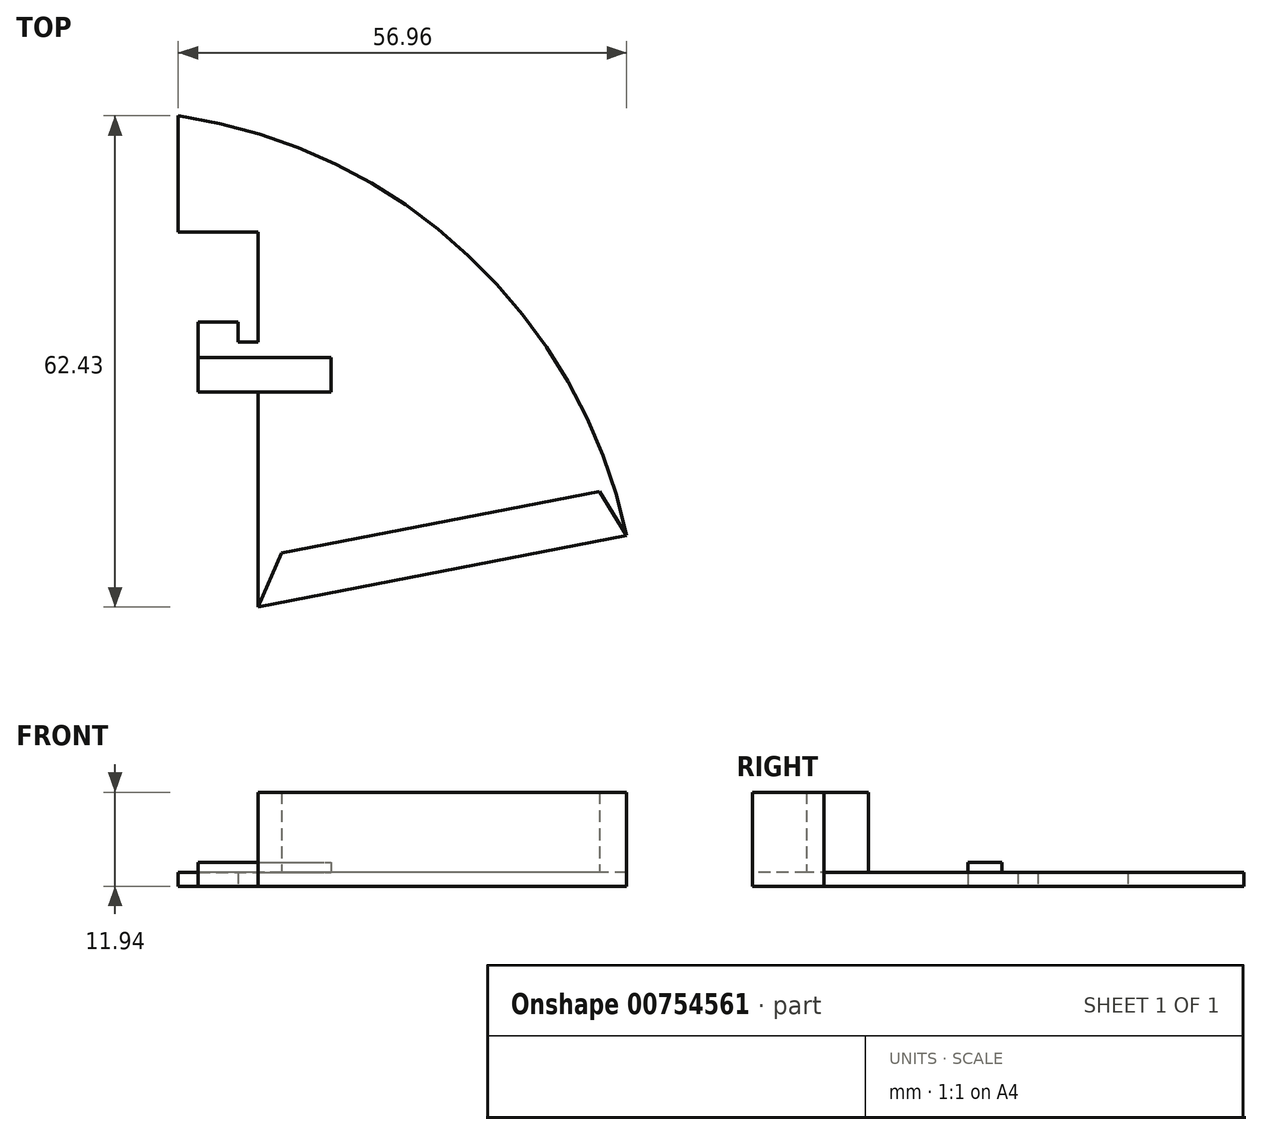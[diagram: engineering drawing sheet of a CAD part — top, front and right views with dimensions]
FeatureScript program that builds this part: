
annotation { "Feature Type Name" : "Feature", "Feature Type Description" : "" }
export const myFeature = defineFeature(function(context is Context, id is Id, definition is map)
    precondition{}
    {
        {
            var Q0;
            Q0=qCreatedBy(makeId("Top.planeOp"),FACE);
            var sketch = newSketch(context, id + "F0", { "sketchPlane" : qUnion([Q0])});
            skLineSegment(sketch, "E0", {"start": v(0, 0) * mm, "end": v(0, 27.36) * mm});
            skLineSegment(sketch, "E1", {"start": v(0, 47.68) * mm, "end": v(-10.16, 47.68) * mm});
            skLineSegment(sketch, "E2", {"start": v(-10.16, 47.68) * mm, "end": v(-10.16, 62.43) * mm});
            skLineSegment(sketch, "E3", {"start": v(0, 0) * mm, "end": v(46.8, 9.1) * mm});
            skArc(sketch, "E4", {"start": v(46.8, 9.1) * mm, "mid": v(26.69, 44.7) * mm, "end": v(-10.16, 62.43) * mm});
            skLineSegment(sketch, "E5", {"start": v(0, 33.7) * mm, "end": v(-2.54, 33.7) * mm});
            skLineSegment(sketch, "E6", {"start": v(-2.54, 33.7) * mm, "end": v(-2.54, 36.25) * mm});
            skLineSegment(sketch, "E7", {"start": v(-2.54, 36.25) * mm, "end": v(-7.62, 36.25) * mm});
            skLineSegment(sketch, "E8", {"start": v(-7.62, 36.25) * mm, "end": v(-7.62, 27.36) * mm});
            skLineSegment(sketch, "E9", {"start": v(-7.62, 27.36) * mm, "end": v(0, 27.36) * mm});
            skLineSegment(sketch, "E10.trimOffspring", {"start": v(0, 33.7) * mm, "end": v(0, 47.68) * mm});
            skSolve(sketch);
        }
        {
            var Q0;
            Q0 = qSketchRegion(id + "F0", true);
            extrude(context, id + "F1", {"entities" : qUnion([Q0]), "depth" : 1.78 * mm, "offsetDistance" : 25.4 * mm});
        }
        {
            var Q0;
            Q0=makeQuery(id+"F1.opExtrude","CAP_FACE",FACE,{"disambiguationData":[OSD([sQuery(id+"F0.wireOp",EDGE,"E0"),sQuery(id+"F0.wireOp",EDGE,"E1"),sQuery(id+"F0.wireOp",EDGE,"E2"),sQuery(id+"F0.wireOp",EDGE,"E3"),sQuery(id+"F0.wireOp",EDGE,"E4"),sQuery(id+"F0.wireOp",EDGE,"E5"),sQuery(id+"F0.wireOp",EDGE,"E6"),sQuery(id+"F0.wireOp",EDGE,"E7"),sQuery(id+"F0.wireOp",EDGE,"E8"),sQuery(id+"F0.wireOp",EDGE,"E9"),sQuery(id+"F0.wireOp",EDGE,"E10.trimOffspring")])],"isStart":false});
            var sketch = newSketch(context, id + "F2", { "sketchPlane" : qUnion([Q0])});
            skLineSegment(sketch, "E11", {"start": v(0, 0) * mm, "end": v(46.8, 9.1) * mm});
            skLineSegment(sketch, "E12", {"start": v(46.8, 9.1) * mm, "end": v(43.36, 14.7) * mm});
            skLineSegment(sketch, "E13", {"start": v(43.36, 14.7) * mm, "end": v(2.99, 6.87) * mm});
            skLineSegment(sketch, "E14", {"start": v(2.99, 6.87) * mm, "end": v(0, 0) * mm});
            skSolve(sketch);
        }
        {
            var Q0;
            Q0 = qSketchRegion(id + "F2", true);
            extrude(context, id + "F3", {"entities" : qUnion([Q0]), "operationType" : NewBodyOperationType.ADD, "depth" : 10.16 * mm, "offsetDistance" : 25.4 * mm});
        }
        {
            var Q0;
            Q0=makeQuery(id+"F1.opExtrude","CAP_FACE",FACE,{"disambiguationData":[OSD([sQuery(id+"F0.wireOp",EDGE,"E0"),sQuery(id+"F0.wireOp",EDGE,"E1"),sQuery(id+"F0.wireOp",EDGE,"E2"),sQuery(id+"F0.wireOp",EDGE,"E3"),sQuery(id+"F0.wireOp",EDGE,"E4"),sQuery(id+"F0.wireOp",EDGE,"E5"),sQuery(id+"F0.wireOp",EDGE,"E6"),sQuery(id+"F0.wireOp",EDGE,"E7"),sQuery(id+"F0.wireOp",EDGE,"E8"),sQuery(id+"F0.wireOp",EDGE,"E9"),sQuery(id+"F0.wireOp",EDGE,"E10.trimOffspring")])],"isStart":false});
            var sketch = newSketch(context, id + "F4", { "sketchPlane" : qUnion([Q0])});
            skLineSegment(sketch, "E15.bottom", {"start": v(-7.62, 27.36) * mm, "end": v(9.24, 27.36) * mm});
            skLineSegment(sketch, "E15.top", {"start": v(-7.62, 31.7) * mm, "end": v(9.24, 31.7) * mm});
            skLineSegment(sketch, "E15.left", {"start": v(-7.62, 27.36) * mm, "end": v(-7.62, 31.7) * mm});
            skLineSegment(sketch, "E15.right", {"start": v(9.24, 27.36) * mm, "end": v(9.24, 31.7) * mm});
            skSolve(sketch);
        }
        {
            var Q0;
            Q0 = qSketchRegion(id + "F4", true);
            extrude(context, id + "F5", {"entities" : qUnion([Q0]), "operationType" : NewBodyOperationType.ADD, "depth" : 1.27 * mm, "offsetDistance" : 25.4 * mm});
        }
    });
